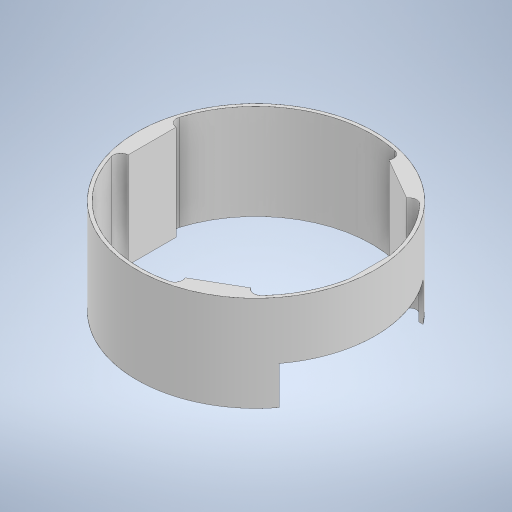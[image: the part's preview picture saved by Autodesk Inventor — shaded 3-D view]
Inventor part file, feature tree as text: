
AUTODESK INVENTOR PART (.ipt)
format: ipt  version: 2023 (Build 270158000, 158)  size: 295,936 bytes
history: native  units: mm
features: extrude x4, sketch x4, other x1, fillet x1
ambient origin geometry x8: Origin, YZ Plane, XZ Plane, XY Plane, X Axis, Y Axis, Z Axis, Center Point
bodies: Body1 (feature_tree)
feature tree (10):
  other  "ソリッド1"
  extrude  "押し出し1"  Depth=250.0mm
  fillet  "フィレット1"  Radius=243.0mm
  extrude  "押し出し4"  Depth=118.86mm
  extrude  "押し出し5"  Depth=10.0mm
  extrude  "押し出し6"  Depth=30.0mm TaperAngle=360.0deg
  sketch  "スケッチ1"
  sketch  "スケッチ4"
  sketch  "スケッチ5"
  sketch  "スケッチ6"
